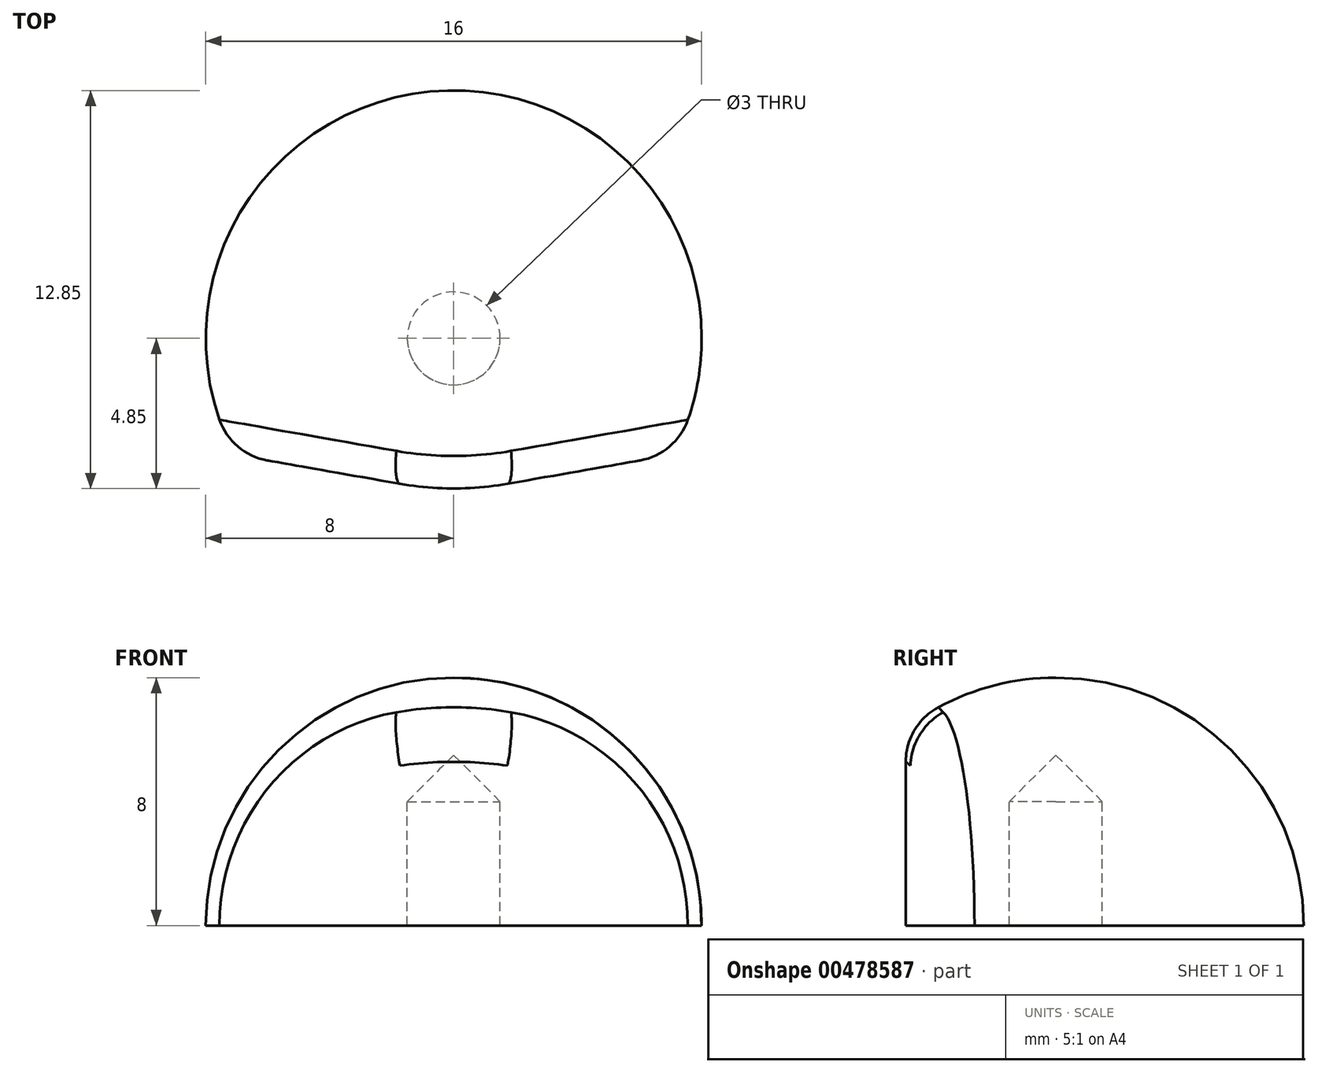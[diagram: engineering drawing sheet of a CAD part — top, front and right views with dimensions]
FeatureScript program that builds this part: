
annotation { "Feature Type Name" : "Feature", "Feature Type Description" : "" }
export const myFeature = defineFeature(function(context is Context, id is Id, definition is map)
    precondition{}
    {
        {
            var Q0;
            Q0=qCreatedBy(makeId("Front.planeOp"),FACE);
            var sketch = newSketch(context, id + "F0", { "sketchPlane" : qUnion([Q0])});
            skLineSegment(sketch, "E0", {"start": v(1.5, 4) * mm, "end": v(1.5, 0) * mm});
            skLineSegment(sketch, "E1", {"start": v(1.5, 4) * mm, "end": v(0, 5.5) * mm});
            skLineSegment(sketch, "E2", {"start": v(1.5, 0) * mm, "end": v(8, 0) * mm});
            skLineSegment(sketch, "E3", {"start": v(1.5, 0) * mm, "end": v(0, 0) * mm, "construction": true});
            skLineSegment(sketch, "E4", {"start": v(0, 5.5) * mm, "end": v(0, 0) * mm, "construction": true});
            skArc(sketch, "E5", {"start": v(8, 0) * mm, "mid": v(5.66, 5.66) * mm, "end": v(0, 8) * mm});
            skLineSegment(sketch, "E6", {"start": v(0, 5.5) * mm, "end": v(0, 8) * mm});
            skSolve(sketch);
        }
        {
            var Q0;
            Q0 = qSketchRegion(id + "F0", true);
            var Q1;
            Q1=sQuery(id+"F0.wireOp",EDGE,"E4");
            revolve(context, id + "F1", {"entities" : qUnion([Q0]), "axis" : qUnion([Q1]), "revolveType" : RevolveType.FULL});
        }
        {
            var Q0;
            Q0=qCreatedBy(makeId("Top.planeOp"),FACE);
            var sketch = newSketch(context, id + "F2", { "sketchPlane" : qUnion([Q0])});
            skLineSegment(sketch, "E7", {"start": v(0, 0) * mm, "end": v(0, -5) * mm, "construction": true});
            skLineSegment(sketch, "E8", {"start": v(0, -5) * mm, "end": v(-28.36, 0) * mm});
            skLineSegment(sketch, "E9", {"start": v(-28.36, 0) * mm, "end": v(-28.36, -16.38) * mm});
            skLineSegment(sketch, "E10", {"start": v(-28.36, -16.38) * mm, "end": v(0, -16.38) * mm});
            skLineSegment(sketch, "E11.MirrorCS", {"start": v(0, -5) * mm, "end": v(28.36, 0) * mm});
            skLineSegment(sketch, "E12.MirrorCS", {"start": v(28.36, -16.38) * mm, "end": v(0, -16.38) * mm});
            skLineSegment(sketch, "E13.MirrorCS", {"start": v(28.36, 0) * mm, "end": v(28.36, -16.38) * mm});
            skSolve(sketch);
        }
        {
            var Q0;
            Q0 = qSketchRegion(id + "F2", true);
            extrude(context, id + "F3", {"entities" : qUnion([Q0]), "operationType" : NewBodyOperationType.REMOVE, "depth" : 25 * mm, "offsetDistance" : 25 * mm});
        }
        {
            var Q0;
            Q0=makeQuery(id+"F3.boolean.opBoolean","COPY",EDGE,{"derivedFrom":makeQuery(id+"F3.opExtrude","SWEPT_EDGE",EDGE,{"disambiguationData":[OSD([sQuery(id+"F2.wireOp",EDGE,"E8"),sQuery(id+"F2.wireOp",EDGE,"E11.MirrorCS")])]})});
            fillet(context, id + "F4", {"entities" : qUnion([Q0]), "radius" : 10 * mm, "tangentPropagation" : true, "allowEdgeOverflow" : false});
        }
        {
            var Q0;
            Q0=makeQuery(id+"F3.boolean.opBoolean","INTERSECT",EDGE,{"derivedFrom":[makeQuery(id+"F1.opRevolve","SWEPT_FACE",FACE,{"disambiguationData":[OSD([sQuery(id+"F0.wireOp",EDGE,"E5")])]}),makeQuery(id+"F3.opExtrude","SWEPT_FACE",FACE,{"disambiguationData":[OSD([sQuery(id+"F2.wireOp",EDGE,"E8")])]})]});
            fillet(context, id + "F5", {"entities" : qUnion([Q0]), "radius" : 2 * mm, "tangentPropagation" : true, "allowEdgeOverflow" : false});
        }
    });
